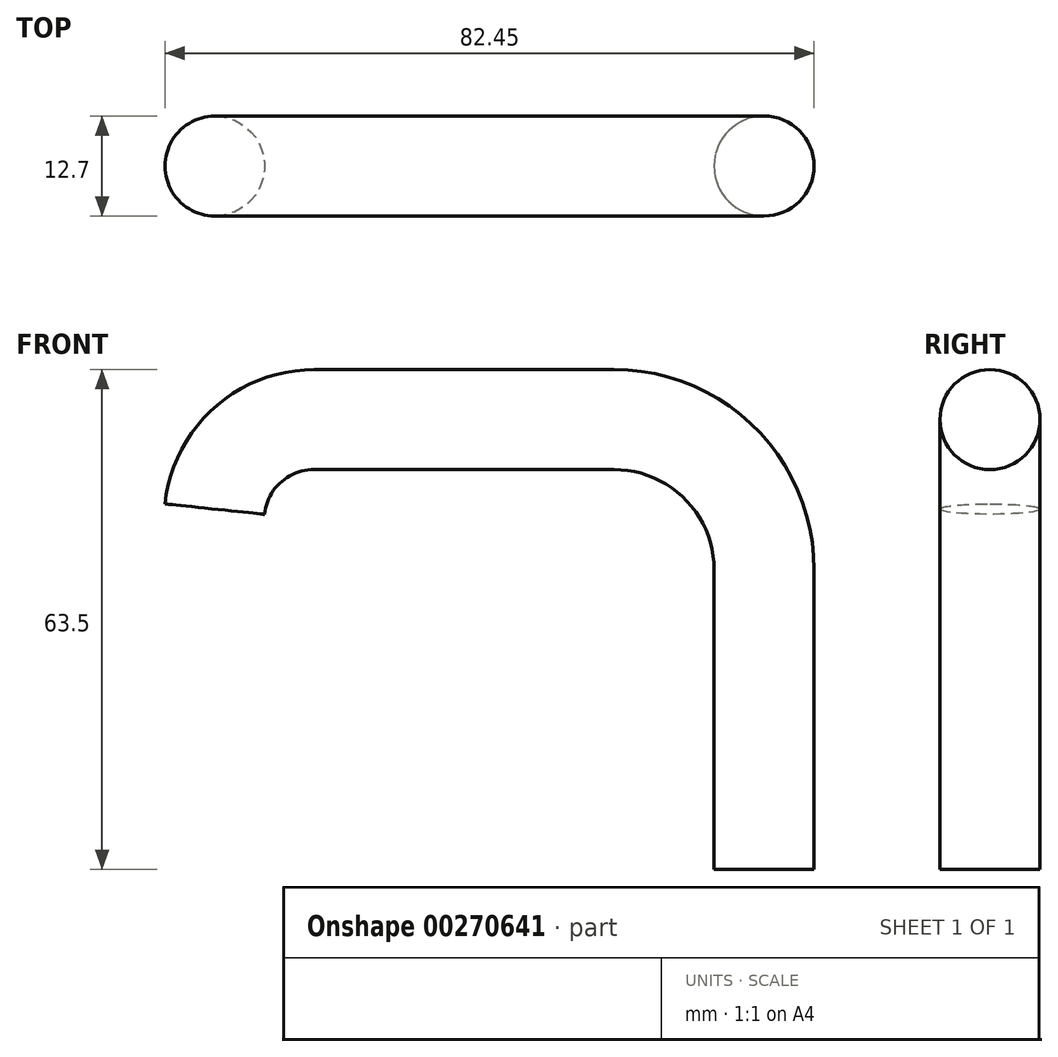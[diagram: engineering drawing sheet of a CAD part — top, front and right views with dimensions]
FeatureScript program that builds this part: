
annotation { "Feature Type Name" : "Feature", "Feature Type Description" : "" }
export const myFeature = defineFeature(function(context is Context, id is Id, definition is map)
    precondition{}
    {
        {
            var Q0;
            Q0=qCreatedBy(makeId("Top.planeOp"),FACE);
            var sketch = newSketch(context, id + "F0", { "sketchPlane" : qUnion([Q0])});
            skCircle(sketch, "E0", {"center": v(0, 0) * mm, "radius": 6.35 * mm});
            skSolve(sketch);
        }
        {
            var Q0;
            Q0=qCreatedBy(makeId("Front.planeOp"),FACE);
            var sketch = newSketch(context, id + "F1", { "sketchPlane" : qUnion([Q0])});
            skLineSegment(sketch, "E1", {"start": v(0, 0) * mm, "end": v(0, 38.1) * mm});
            skArc(sketch, "E2", {"start": v(0, 38.1) * mm, "mid": v(-5.58, 51.57) * mm, "end": v(-19.05, 57.15) * mm});
            skLineSegment(sketch, "E3", {"start": v(-19.05, 57.15) * mm, "end": v(-57.15, 57.15) * mm});
            skArc(sketch, "E4", {"start": v(-57.15, 57.15) * mm, "mid": v(-65.65, 53.89) * mm, "end": v(-69.78, 45.77) * mm});
            skSolve(sketch);
        }
        {
            var Q0;
            Q0=makeQuery(id+"F0.imprint","IMPRINT",FACE,{"disambiguationData":[TD([[makeQuery(id+"F0.imprint","IMPRINT",EDGE,{"derivedFrom":sQuery(id+"F0.wireOp",EDGE,"E0")}),1.0]])]});
            var Q1;
            Q1=sQuery(id+"F1.wireOp",EDGE,"E1");
            var Q2;
            Q2=sQuery(id+"F1.wireOp",EDGE,"E2");
            var Q3;
            Q3=sQuery(id+"F1.wireOp",EDGE,"E3");
            var Q4;
            Q4=sQuery(id+"F1.wireOp",EDGE,"E4");
            sweep(context, id + "F2", {"profiles" : qUnion([Q0]), "path" : qUnion([Q1, Q2, Q3, Q4])});
        }
    });
